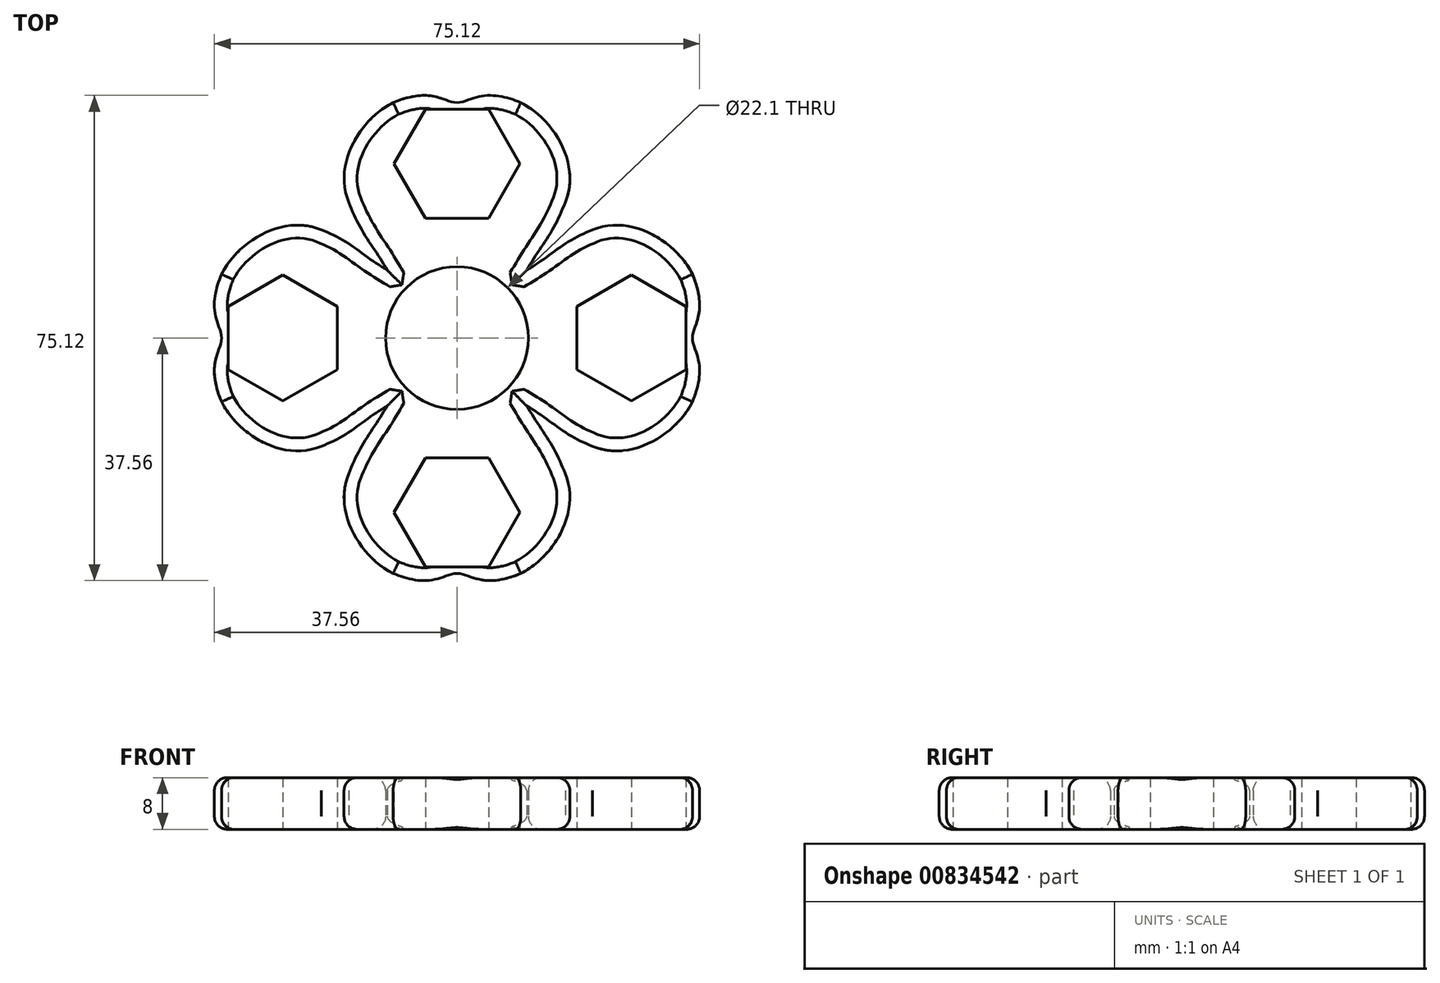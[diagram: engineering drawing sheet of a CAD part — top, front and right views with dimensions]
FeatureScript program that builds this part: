
annotation { "Feature Type Name" : "Feature", "Feature Type Description" : "" }
export const myFeature = defineFeature(function(context is Context, id is Id, definition is map)
    precondition{}
    {
        {
            var Q0;
            Q0=qCreatedBy(makeId("Top.planeOp"),FACE);
            var sketch = newSketch(context, id + "F0", { "sketchPlane" : qUnion([Q0])});
            skCircle(sketch, "E0", {"center": v(0, 0) * mm, "radius": 11.05 * mm});
            skCircle(sketch, "E1.cCircle", {"center": v(27, 0) * mm, "radius": 8.45 * mm, "construction": true});
            skLineSegment(sketch, "E1.0", {"start": v(27, 9.76) * mm, "end": v(35.45, 4.88) * mm});
            skLineSegment(sketch, "E1.1", {"start": v(35.45, 4.88) * mm, "end": v(35.45, -4.88) * mm});
            skLineSegment(sketch, "E1.2", {"start": v(35.45, -4.88) * mm, "end": v(27, -9.76) * mm});
            skLineSegment(sketch, "E1.3", {"start": v(27, -9.76) * mm, "end": v(18.55, -4.88) * mm});
            skLineSegment(sketch, "E1.4", {"start": v(18.55, -4.88) * mm, "end": v(18.55, 4.88) * mm});
            skLineSegment(sketch, "E1.5", {"start": v(18.55, 4.88) * mm, "end": v(27, 9.76) * mm});
            skPoint(sketch, "E1.0.midPoint", {"position": v(31.22, 7.32) * mm});
            skLineSegment(sketch, "E2.1.0", {"start": v(-4.88, 18.55) * mm, "end": v(-9.76, 27) * mm});
            skLineSegment(sketch, "E2.1.1", {"start": v(4.88, 18.55) * mm, "end": v(-4.88, 18.55) * mm});
            skLineSegment(sketch, "E2.1.2", {"start": v(-9.76, 27) * mm, "end": v(-4.88, 35.45) * mm});
            skLineSegment(sketch, "E2.1.3", {"start": v(-4.88, 35.45) * mm, "end": v(4.88, 35.45) * mm});
            skLineSegment(sketch, "E2.1.4", {"start": v(4.88, 35.45) * mm, "end": v(9.76, 27) * mm});
            skLineSegment(sketch, "E2.1.5", {"start": v(9.76, 27) * mm, "end": v(4.88, 18.55) * mm});
            skLineSegment(sketch, "E2.2.0", {"start": v(-18.55, -4.88) * mm, "end": v(-27, -9.76) * mm});
            skLineSegment(sketch, "E2.2.1", {"start": v(-18.55, 4.88) * mm, "end": v(-18.55, -4.88) * mm});
            skLineSegment(sketch, "E2.2.2", {"start": v(-27, -9.76) * mm, "end": v(-35.45, -4.88) * mm});
            skLineSegment(sketch, "E2.2.3", {"start": v(-35.45, -4.88) * mm, "end": v(-35.45, 4.88) * mm});
            skLineSegment(sketch, "E2.2.4", {"start": v(-35.45, 4.88) * mm, "end": v(-27, 9.76) * mm});
            skLineSegment(sketch, "E2.2.5", {"start": v(-27, 9.76) * mm, "end": v(-18.55, 4.88) * mm});
            skLineSegment(sketch, "E2.3.0", {"start": v(4.88, -18.55) * mm, "end": v(9.76, -27) * mm});
            skLineSegment(sketch, "E2.3.1", {"start": v(-4.88, -18.55) * mm, "end": v(4.88, -18.55) * mm});
            skLineSegment(sketch, "E2.3.2", {"start": v(9.76, -27) * mm, "end": v(4.88, -35.45) * mm});
            skLineSegment(sketch, "E2.3.3", {"start": v(4.88, -35.45) * mm, "end": v(-4.88, -35.45) * mm});
            skLineSegment(sketch, "E2.3.4", {"start": v(-4.88, -35.45) * mm, "end": v(-9.76, -27) * mm});
            skLineSegment(sketch, "E2.3.5", {"start": v(-9.76, -27) * mm, "end": v(-4.88, -18.55) * mm});
            skLineSegment(sketch, "E3", {"start": v(-4.88, 35.45) * mm, "end": v(4.88, 18.55) * mm, "construction": true});
            skLineSegment(sketch, "E4", {"start": v(-35.45, 4.88) * mm, "end": v(-18.55, -4.88) * mm, "construction": true});
            skLineSegment(sketch, "E5", {"start": v(-4.88, -18.55) * mm, "end": v(4.88, -35.45) * mm, "construction": true});
            skPoint(sketch, "E6", {"position": v(0, 27) * mm});
            skPoint(sketch, "E7", {"position": v(-27, 0) * mm});
            skPoint(sketch, "E8", {"position": v(0, -27) * mm});
            skSolve(sketch);
        }
        {
            var Q0;
            Q0=qCreatedBy(makeId("Top.planeOp"),FACE);
            var sketch = newSketch(context, id + "F1", { "sketchPlane" : qUnion([Q0])});
            skLineSegment(sketch, "E9.0.0", {"start": v(4.88, 18.55) * mm, "end": v(9.76, 27) * mm});
            skLineSegment(sketch, "E9.0.1", {"start": v(9.76, 27) * mm, "end": v(4.88, 35.45) * mm});
            skLineSegment(sketch, "E9.0.2", {"start": v(4.88, 35.45) * mm, "end": v(-4.88, 35.45) * mm});
            skLineSegment(sketch, "E9.0.3", {"start": v(-4.88, 35.45) * mm, "end": v(-9.76, 27) * mm});
            skLineSegment(sketch, "E9.0.4", {"start": v(-9.76, 27) * mm, "end": v(-4.88, 18.55) * mm});
            skLineSegment(sketch, "E9.0.5", {"start": v(-4.88, 18.55) * mm, "end": v(4.88, 18.55) * mm});
            skLineSegment(sketch, "E10.0.0", {"start": v(-18.55, 4.88) * mm, "end": v(-27, 9.76) * mm});
            skLineSegment(sketch, "E10.0.1", {"start": v(-27, 9.76) * mm, "end": v(-35.45, 4.88) * mm});
            skLineSegment(sketch, "E10.0.2", {"start": v(-35.45, 4.88) * mm, "end": v(-35.45, -4.88) * mm});
            skLineSegment(sketch, "E10.0.3", {"start": v(-35.45, -4.88) * mm, "end": v(-27, -9.76) * mm});
            skLineSegment(sketch, "E10.0.4", {"start": v(-27, -9.76) * mm, "end": v(-18.55, -4.88) * mm});
            skLineSegment(sketch, "E10.0.5", {"start": v(-18.55, -4.88) * mm, "end": v(-18.55, 4.88) * mm});
            skCircle(sketch, "E11.0.0", {"center": v(0, 0) * mm, "radius": 11.05 * mm});
            skLineSegment(sketch, "E12.0.0", {"start": v(27, 9.76) * mm, "end": v(18.55, 4.88) * mm});
            skLineSegment(sketch, "E12.0.1", {"start": v(18.55, 4.88) * mm, "end": v(18.55, -4.88) * mm});
            skLineSegment(sketch, "E12.0.2", {"start": v(18.55, -4.88) * mm, "end": v(27, -9.76) * mm});
            skLineSegment(sketch, "E12.0.3", {"start": v(27, -9.76) * mm, "end": v(35.45, -4.88) * mm});
            skLineSegment(sketch, "E12.0.4", {"start": v(35.45, -4.88) * mm, "end": v(35.45, 4.88) * mm});
            skLineSegment(sketch, "E12.0.5", {"start": v(35.45, 4.88) * mm, "end": v(27, 9.76) * mm});
            skLineSegment(sketch, "E13.0.0", {"start": v(-4.88, -18.55) * mm, "end": v(-9.76, -27) * mm});
            skLineSegment(sketch, "E13.0.1", {"start": v(-9.76, -27) * mm, "end": v(-4.88, -35.45) * mm});
            skLineSegment(sketch, "E13.0.2", {"start": v(-4.88, -35.45) * mm, "end": v(4.88, -35.45) * mm});
            skLineSegment(sketch, "E13.0.3", {"start": v(4.88, -35.45) * mm, "end": v(9.76, -27) * mm});
            skLineSegment(sketch, "E13.0.4", {"start": v(9.76, -27) * mm, "end": v(4.88, -18.55) * mm});
            skLineSegment(sketch, "E13.0.5", {"start": v(4.88, -18.55) * mm, "end": v(-4.88, -18.55) * mm});
            skLineSegment(sketch, "E14", {"start": v(25, 9.76) * mm, "end": v(25, -9.76) * mm, "construction": true});
            skCircle(sketch, "E15.0", {"center": v(0, 0) * mm, "radius": 15.05 * mm});
            skFitSpline(sketch, "E16", {"points": [v(10.78, 10.5) * mm, v(21, 16.76) * mm], "startDerivative": vector(15, 9) * mm, "endDerivative": vector(15, 6) * mm});
            skFitSpline(sketch, "E17", {"points": [v(21, 16.76) * mm, v(36.45, 9.88) * mm], "startDerivative": vector(18, 7.5) * mm, "endDerivative": vector(7.5, -15) * mm});
            skFitSpline(sketch, "E18", {"points": [v(36.45, 9.88) * mm, v(36.45, 0) * mm], "startDerivative": vector(7.5, -18) * mm, "endDerivative": vector(0, -6) * mm});
            skFitSpline(sketch, "E19.MirrorCS", {"points": [v(10.78, -10.5) * mm, v(21, -16.76) * mm], "startDerivative": vector(15, -9) * mm, "endDerivative": vector(15, -6) * mm});
            skFitSpline(sketch, "E20.MirrorCS", {"points": [v(21, -16.76) * mm, v(36.45, -9.88) * mm], "startDerivative": vector(18, -7.5) * mm, "endDerivative": vector(7.5, 15) * mm});
            skFitSpline(sketch, "E21.MirrorCS", {"points": [v(36.45, -9.88) * mm, v(36.45, 0) * mm], "startDerivative": vector(7.5, 18) * mm, "endDerivative": vector(0, 6) * mm});
            skFitSpline(sketch, "E22.MirrorCS", {"points": [v(-10.78, -10.5) * mm, v(-21, -16.76) * mm], "startDerivative": vector(-15, -9) * mm, "endDerivative": vector(-15, -6) * mm});
            skFitSpline(sketch, "E23.MirrorCS", {"points": [v(-21, -16.76) * mm, v(-36.45, -9.88) * mm], "startDerivative": vector(-18, -7.5) * mm, "endDerivative": vector(-7.5, 15) * mm});
            skFitSpline(sketch, "E24.MirrorCS", {"points": [v(-36.45, -9.88) * mm, v(-36.45, 0) * mm], "startDerivative": vector(-7.5, 18) * mm, "endDerivative": vector(0, 6) * mm});
            skFitSpline(sketch, "E25.MirrorCS", {"points": [v(-36.45, 9.88) * mm, v(-36.45, 0) * mm], "startDerivative": vector(-7.5, -18) * mm, "endDerivative": vector(0, -6) * mm});
            skFitSpline(sketch, "E26.MirrorCS", {"points": [v(-21, 16.76) * mm, v(-36.45, 9.88) * mm], "startDerivative": vector(-18, 7.5) * mm, "endDerivative": vector(-7.5, -15) * mm});
            skFitSpline(sketch, "E27.MirrorCS", {"points": [v(-10.78, 10.5) * mm, v(-21, 16.76) * mm], "startDerivative": vector(-15, 9) * mm, "endDerivative": vector(-15, 6) * mm});
            skFitSpline(sketch, "E28", {"points": [v(-10.78, 10.5) * mm, v(-16.76, 21) * mm], "startDerivative": vector(-9, 15) * mm, "endDerivative": vector(-6, 15) * mm});
            skFitSpline(sketch, "E29", {"points": [v(-16.76, 21) * mm, v(-9.88, 36.45) * mm], "startDerivative": vector(-7.5, 18) * mm, "endDerivative": vector(15, 7.5) * mm});
            skPoint(sketch, "E30.1.internal.snap0", {"position": v(0, 33.45) * mm});
            skFitSpline(sketch, "E30", {"points": [v(-9.88, 36.45) * mm, v(0, 36.45) * mm], "startDerivative": vector(18, 7.5) * mm, "endDerivative": vector(6, 0) * mm});
            skFitSpline(sketch, "E31.MirrorCS", {"points": [v(10.78, 10.5) * mm, v(16.76, 21) * mm], "startDerivative": vector(9, 15) * mm, "endDerivative": vector(6, 15) * mm});
            skFitSpline(sketch, "E32.MirrorCS", {"points": [v(16.76, 21) * mm, v(9.88, 36.45) * mm], "startDerivative": vector(7.5, 18) * mm, "endDerivative": vector(-15, 7.5) * mm});
            skFitSpline(sketch, "E33.MirrorCS", {"points": [v(9.88, 36.45) * mm, v(0, 36.45) * mm], "startDerivative": vector(-18, 7.5) * mm, "endDerivative": vector(-6, 0) * mm});
            skFitSpline(sketch, "E34.MirrorCS", {"points": [v(-10.78, -10.5) * mm, v(-16.76, -21) * mm], "startDerivative": vector(-9, -15) * mm, "endDerivative": vector(-6, -15) * mm});
            skFitSpline(sketch, "E35.MirrorCS", {"points": [v(-16.76, -21) * mm, v(-9.88, -36.45) * mm], "startDerivative": vector(-7.5, -18) * mm, "endDerivative": vector(15, -7.5) * mm});
            skFitSpline(sketch, "E36.MirrorCS", {"points": [v(-9.88, -36.45) * mm, v(0, -36.45) * mm], "startDerivative": vector(18, -7.5) * mm, "endDerivative": vector(6, 0) * mm});
            skFitSpline(sketch, "E37.MirrorCS", {"points": [v(9.88, -36.45) * mm, v(0, -36.45) * mm], "startDerivative": vector(-18, -7.5) * mm, "endDerivative": vector(-6, 0) * mm});
            skFitSpline(sketch, "E38.MirrorCS", {"points": [v(10.78, -10.5) * mm, v(16.76, -21) * mm], "startDerivative": vector(9, -15) * mm, "endDerivative": vector(6, -15) * mm});
            skFitSpline(sketch, "E39.MirrorCS", {"points": [v(16.76, -21) * mm, v(9.88, -36.45) * mm], "startDerivative": vector(7.5, -18) * mm, "endDerivative": vector(-15, -7.5) * mm});
            skSolve(sketch);
        }
        {
            var Q0;
            Q0=makeQuery(id+"F1.imprint","IMPRINT",FACE,{"disambiguationData":[TD([[makeQuery(id+"F1.imprint","IMPRINT",EDGE,{"derivedFrom":sQuery(id+"F1.wireOp",EDGE,"E10.0.0")}),-1.0]])]});
            var Q1;
            Q1=makeQuery(id+"F1.imprint","IMPRINT",FACE,{"disambiguationData":[TD([[makeQuery(id+"F1.imprint","IMPRINT",EDGE,{"derivedFrom":sQuery(id+"F1.wireOp",EDGE,"E9.0.0")}),-1.0]])]});
            var Q2;
            Q2=makeQuery(id+"F1.imprint","IMPRINT",FACE,{"disambiguationData":[TD([[makeQuery(id+"F1.imprint","IMPRINT",EDGE,{"derivedFrom":sQuery(id+"F1.wireOp",EDGE,"E12.0.0")}),-1.0]])]});
            var Q3;
            Q3=makeQuery(id+"F1.imprint","IMPRINT",FACE,{"disambiguationData":[TD([[makeQuery(id+"F1.imprint","IMPRINT",EDGE,{"derivedFrom":sQuery(id+"F1.wireOp",EDGE,"E13.0.0")}),-1.0]])]});
            var Q4;
            Q4=makeQuery(id+"F1.imprint","IMPRINT",FACE,{"disambiguationData":[TD([[makeQuery(id+"F1.imprint","IMPRINT",EDGE,{"derivedFrom":sQuery(id+"F1.wireOp",EDGE,"E11.0.0")}),-1.0]])]});
            extrude(context, id + "F2", {"entities" : qUnion([Q0, Q1, Q2, Q3, Q4]), "depth" : 8 * mm, "offsetDistance" : 25 * mm});
        }
        {
            var Q0;
            Q0=makeQuery(id+"F2.opExtrude","CAP_EDGE",EDGE,{"disambiguationData":[OSD([sQuery(id+"F1.wireOp",EDGE,"E23.MirrorCS")])],"isStart":false});
            var Q1;
            Q1=makeQuery(id+"F2.opExtrude","CAP_EDGE",EDGE,{"disambiguationData":[OSD([sQuery(id+"F1.wireOp",EDGE,"E22.MirrorCS")])],"isStart":false});
            var Q2;
            Q2=makeQuery(id+"F2.opExtrude","CAP_EDGE",EDGE,{"disambiguationData":[OSD([sQuery(id+"F1.wireOp",EDGE,"E34.MirrorCS")])],"isStart":false});
            var Q3;
            Q3=makeQuery(id+"F2.opExtrude","CAP_EDGE",EDGE,{"disambiguationData":[OSD([sQuery(id+"F1.wireOp",EDGE,"E36.MirrorCS")])],"isStart":false});
            var Q4;
            Q4=makeQuery(id+"F2.opExtrude","CAP_EDGE",EDGE,{"disambiguationData":[OSD([sQuery(id+"F1.wireOp",EDGE,"E35.MirrorCS")])],"isStart":false});
            var Q5;
            Q5=makeQuery(id+"F2.opExtrude","CAP_EDGE",EDGE,{"disambiguationData":[OSD([sQuery(id+"F1.wireOp",EDGE,"E37.MirrorCS")])],"isStart":false});
            var Q6;
            Q6=makeQuery(id+"F2.opExtrude","CAP_EDGE",EDGE,{"disambiguationData":[OSD([sQuery(id+"F1.wireOp",EDGE,"E39.MirrorCS")])],"isStart":false});
            var Q7;
            Q7=makeQuery(id+"F2.opExtrude","CAP_EDGE",EDGE,{"disambiguationData":[OSD([sQuery(id+"F1.wireOp",EDGE,"E38.MirrorCS")])],"isStart":false});
            var Q8;
            Q8=makeQuery(id+"F2.opExtrude","CAP_EDGE",EDGE,{"disambiguationData":[OSD([sQuery(id+"F1.wireOp",EDGE,"E19.MirrorCS")])],"isStart":false});
            var Q9;
            Q9=makeQuery(id+"F2.opExtrude","CAP_EDGE",EDGE,{"disambiguationData":[OSD([sQuery(id+"F1.wireOp",EDGE,"E20.MirrorCS")])],"isStart":false});
            var Q10;
            Q10=makeQuery(id+"F2.opExtrude","CAP_EDGE",EDGE,{"disambiguationData":[OSD([sQuery(id+"F1.wireOp",EDGE,"E18")])],"isStart":false});
            var Q11;
            Q11=makeQuery(id+"F2.opExtrude","CAP_EDGE",EDGE,{"disambiguationData":[OSD([sQuery(id+"F1.wireOp",EDGE,"E21.MirrorCS")])],"isStart":false});
            var Q12;
            Q12=makeQuery(id+"F2.opExtrude","CAP_EDGE",EDGE,{"disambiguationData":[OSD([sQuery(id+"F1.wireOp",EDGE,"E17")])],"isStart":false});
            var Q13;
            Q13=makeQuery(id+"F2.opExtrude","CAP_EDGE",EDGE,{"disambiguationData":[OSD([sQuery(id+"F1.wireOp",EDGE,"E16")])],"isStart":false});
            var Q14;
            Q14=makeQuery(id+"F2.opExtrude","CAP_EDGE",EDGE,{"disambiguationData":[OSD([sQuery(id+"F1.wireOp",EDGE,"E31.MirrorCS")])],"isStart":false});
            var Q15;
            Q15=makeQuery(id+"F2.opExtrude","CAP_EDGE",EDGE,{"disambiguationData":[OSD([sQuery(id+"F1.wireOp",EDGE,"E32.MirrorCS")])],"isStart":false});
            var Q16;
            Q16=makeQuery(id+"F2.opExtrude","CAP_EDGE",EDGE,{"disambiguationData":[OSD([sQuery(id+"F1.wireOp",EDGE,"E33.MirrorCS")])],"isStart":false});
            var Q17;
            Q17=makeQuery(id+"F2.opExtrude","CAP_EDGE",EDGE,{"disambiguationData":[OSD([sQuery(id+"F1.wireOp",EDGE,"E30")])],"isStart":false});
            var Q18;
            Q18=makeQuery(id+"F2.opExtrude","CAP_EDGE",EDGE,{"disambiguationData":[OSD([sQuery(id+"F1.wireOp",EDGE,"E29")])],"isStart":false});
            var Q19;
            Q19=makeQuery(id+"F2.opExtrude","CAP_EDGE",EDGE,{"disambiguationData":[OSD([sQuery(id+"F1.wireOp",EDGE,"E28")])],"isStart":false});
            var Q20;
            Q20=makeQuery(id+"F2.opExtrude","CAP_EDGE",EDGE,{"disambiguationData":[OSD([sQuery(id+"F1.wireOp",EDGE,"E27.MirrorCS")])],"isStart":false});
            var Q21;
            Q21=makeQuery(id+"F2.opExtrude","CAP_EDGE",EDGE,{"disambiguationData":[OSD([sQuery(id+"F1.wireOp",EDGE,"E26.MirrorCS")])],"isStart":false});
            var Q22;
            Q22=makeQuery(id+"F2.opExtrude","CAP_EDGE",EDGE,{"disambiguationData":[OSD([sQuery(id+"F1.wireOp",EDGE,"E25.MirrorCS")])],"isStart":false});
            var Q23;
            Q23=makeQuery(id+"F2.opExtrude","CAP_EDGE",EDGE,{"disambiguationData":[OSD([sQuery(id+"F1.wireOp",EDGE,"E24.MirrorCS")])],"isStart":false});
            var Q24;
            Q24=makeQuery(id+"F2.opExtrude","CAP_EDGE",EDGE,{"disambiguationData":[OSD([sQuery(id+"F1.wireOp",EDGE,"E11.0.0")])],"isStart":false});
            var Q25;
            Q25=makeQuery(id+"F2.opExtrude","CAP_EDGE",EDGE,{"disambiguationData":[OSD([sQuery(id+"F1.wireOp",EDGE,"E23.MirrorCS")])],"isStart":true});
            var Q26;
            Q26=makeQuery(id+"F2.opExtrude","CAP_EDGE",EDGE,{"disambiguationData":[OSD([sQuery(id+"F1.wireOp",EDGE,"E22.MirrorCS")])],"isStart":true});
            var Q27;
            Q27=makeQuery(id+"F2.opExtrude","CAP_EDGE",EDGE,{"disambiguationData":[OSD([sQuery(id+"F1.wireOp",EDGE,"E34.MirrorCS")])],"isStart":true});
            var Q28;
            Q28=makeQuery(id+"F2.opExtrude","CAP_EDGE",EDGE,{"disambiguationData":[OSD([sQuery(id+"F1.wireOp",EDGE,"E24.MirrorCS")])],"isStart":true});
            var Q29;
            Q29=makeQuery(id+"F2.opExtrude","CAP_EDGE",EDGE,{"disambiguationData":[OSD([sQuery(id+"F1.wireOp",EDGE,"E25.MirrorCS")])],"isStart":true});
            var Q30;
            Q30=makeQuery(id+"F2.opExtrude","CAP_EDGE",EDGE,{"disambiguationData":[OSD([sQuery(id+"F1.wireOp",EDGE,"E26.MirrorCS")])],"isStart":true});
            var Q31;
            Q31=makeQuery(id+"F2.opExtrude","CAP_EDGE",EDGE,{"disambiguationData":[OSD([sQuery(id+"F1.wireOp",EDGE,"E27.MirrorCS")])],"isStart":true});
            var Q32;
            Q32=makeQuery(id+"F2.opExtrude","CAP_EDGE",EDGE,{"disambiguationData":[OSD([sQuery(id+"F1.wireOp",EDGE,"E28")])],"isStart":true});
            var Q33;
            Q33=makeQuery(id+"F2.opExtrude","CAP_EDGE",EDGE,{"disambiguationData":[OSD([sQuery(id+"F1.wireOp",EDGE,"E29")])],"isStart":true});
            var Q34;
            Q34=makeQuery(id+"F2.opExtrude","CAP_EDGE",EDGE,{"disambiguationData":[OSD([sQuery(id+"F1.wireOp",EDGE,"E30")])],"isStart":true});
            var Q35;
            Q35=makeQuery(id+"F2.opExtrude","CAP_EDGE",EDGE,{"disambiguationData":[OSD([sQuery(id+"F1.wireOp",EDGE,"E33.MirrorCS")])],"isStart":true});
            var Q36;
            Q36=makeQuery(id+"F2.opExtrude","CAP_EDGE",EDGE,{"disambiguationData":[OSD([sQuery(id+"F1.wireOp",EDGE,"E32.MirrorCS")])],"isStart":true});
            var Q37;
            Q37=makeQuery(id+"F2.opExtrude","CAP_EDGE",EDGE,{"disambiguationData":[OSD([sQuery(id+"F1.wireOp",EDGE,"E31.MirrorCS")])],"isStart":true});
            var Q38;
            Q38=makeQuery(id+"F2.opExtrude","CAP_EDGE",EDGE,{"disambiguationData":[OSD([sQuery(id+"F1.wireOp",EDGE,"E16")])],"isStart":true});
            var Q39;
            Q39=makeQuery(id+"F2.opExtrude","CAP_EDGE",EDGE,{"disambiguationData":[OSD([sQuery(id+"F1.wireOp",EDGE,"E17")])],"isStart":true});
            var Q40;
            Q40=makeQuery(id+"F2.opExtrude","CAP_EDGE",EDGE,{"disambiguationData":[OSD([sQuery(id+"F1.wireOp",EDGE,"E11.0.0")])],"isStart":true});
            var Q41;
            Q41=makeQuery(id+"F2.opExtrude","CAP_EDGE",EDGE,{"disambiguationData":[OSD([sQuery(id+"F1.wireOp",EDGE,"E18")])],"isStart":true});
            var Q42;
            Q42=makeQuery(id+"F2.opExtrude","CAP_EDGE",EDGE,{"disambiguationData":[OSD([sQuery(id+"F1.wireOp",EDGE,"E21.MirrorCS")])],"isStart":true});
            var Q43;
            Q43=makeQuery(id+"F2.opExtrude","CAP_EDGE",EDGE,{"disambiguationData":[OSD([sQuery(id+"F1.wireOp",EDGE,"E35.MirrorCS")])],"isStart":true});
            var Q44;
            Q44=makeQuery(id+"F2.opExtrude","CAP_EDGE",EDGE,{"disambiguationData":[OSD([sQuery(id+"F1.wireOp",EDGE,"E36.MirrorCS")])],"isStart":true});
            var Q45;
            Q45=makeQuery(id+"F2.opExtrude","CAP_EDGE",EDGE,{"disambiguationData":[OSD([sQuery(id+"F1.wireOp",EDGE,"E37.MirrorCS")])],"isStart":true});
            var Q46;
            Q46=makeQuery(id+"F2.opExtrude","CAP_EDGE",EDGE,{"disambiguationData":[OSD([sQuery(id+"F1.wireOp",EDGE,"E39.MirrorCS")])],"isStart":true});
            var Q47;
            Q47=makeQuery(id+"F2.opExtrude","CAP_EDGE",EDGE,{"disambiguationData":[OSD([sQuery(id+"F1.wireOp",EDGE,"E38.MirrorCS")])],"isStart":true});
            var Q48;
            Q48=makeQuery(id+"F2.opExtrude","CAP_EDGE",EDGE,{"disambiguationData":[OSD([sQuery(id+"F1.wireOp",EDGE,"E19.MirrorCS")])],"isStart":true});
            var Q49;
            Q49=makeQuery(id+"F2.opExtrude","CAP_EDGE",EDGE,{"disambiguationData":[OSD([sQuery(id+"F1.wireOp",EDGE,"E20.MirrorCS")])],"isStart":true});
            fillet(context, id + "F3", {"entities" : qUnion([Q0, Q1, Q2, Q3, Q4, Q5, Q6, Q7, Q8, Q9, Q10, Q11, Q12, Q13, Q14, Q15, Q16, Q17, Q18, Q19, Q20, Q21, Q22, Q23, Q24, Q25, Q26, Q27, Q28, Q29, Q30, Q31, Q32, Q33, Q34, Q35, Q36, Q37, Q38, Q39, Q40, Q41, Q42, Q43, Q44, Q45, Q46, Q47, Q48, Q49]), "radius" : 2 * mm, "tangentPropagation" : true, "allowEdgeOverflow" : false});
        }
    });
